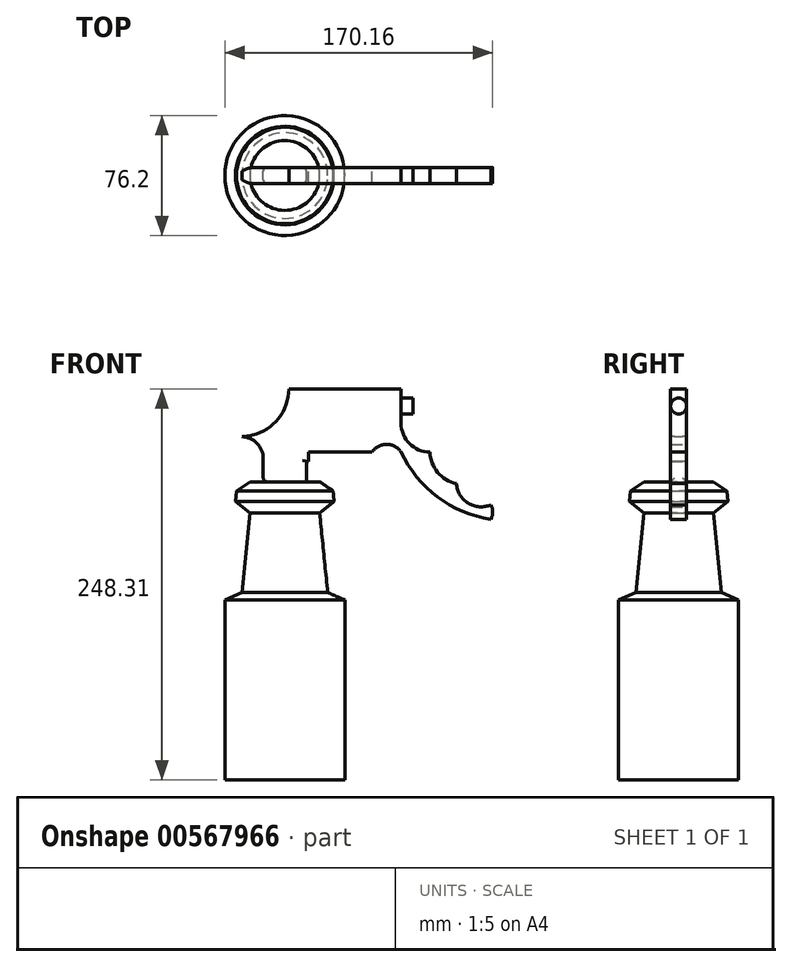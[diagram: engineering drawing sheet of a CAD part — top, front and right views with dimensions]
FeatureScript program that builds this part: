
annotation { "Feature Type Name" : "Feature", "Feature Type Description" : "" }
export const myFeature = defineFeature(function(context is Context, id is Id, definition is map)
    precondition{}
    {
        {
            var Q0;
            Q0=qCreatedBy(makeId("Front.planeOp"),FACE);
            var sketch = newSketch(context, id + "F0", { "sketchPlane" : qUnion([Q0])});
            skLineSegment(sketch, "E0", {"start": v(0, 0) * mm, "end": v(0, 114.3) * mm});
            skLineSegment(sketch, "E1", {"start": v(-38.1, 114.3) * mm, "end": v(-38.1, 0) * mm});
            skLineSegment(sketch, "E2", {"start": v(-38.1, 0) * mm, "end": v(0, 0) * mm});
            skLineSegment(sketch, "E3", {"start": v(0, 114.3) * mm, "end": v(-10.86, 119.11) * mm});
            skLineSegment(sketch, "E4", {"start": v(-38.1, 176.23) * mm, "end": v(-38.1, 114.3) * mm});
            skPoint(sketch, "E5.end.orphan", {"position": v(-25.4, 114.3) * mm});
            skLineSegment(sketch, "E6", {"start": v(-10.86, 119.11) * mm, "end": v(-15.96, 169.65) * mm});
            skLineSegment(sketch, "E7", {"start": v(-15.96, 169.65) * mm, "end": v(-6.76, 176.88) * mm});
            skLineSegment(sketch, "E8", {"start": v(-6.76, 176.88) * mm, "end": v(-7.45, 183.67) * mm});
            skLineSegment(sketch, "E9", {"start": v(-7.45, 183.67) * mm, "end": v(-15.96, 189.42) * mm});
            skLineSegment(sketch, "E10", {"start": v(-15.96, 189.42) * mm, "end": v(-38.1, 189.42) * mm});
            skLineSegment(sketch, "E11", {"start": v(-38.1, 189.42) * mm, "end": v(-38.1, 176.23) * mm});
            skSolve(sketch);
        }
        {
            var Q0;
            Q0=makeQuery(id+"F0.imprint","IMPRINT",FACE,{"disambiguationData":[TD([[makeQuery(id+"F0.imprint","IMPRINT",EDGE,{"derivedFrom":sQuery(id+"F0.wireOp",EDGE,"E0")}),1.0]])]});
            var Q1;
            Q1=sQuery(id+"F0.wireOp",EDGE,"E1");
            revolve(context, id + "F1", {"entities" : qUnion([Q0]), "axis" : qUnion([Q1]), "revolveType" : RevolveType.FULL});
        }
        {
            var Q0;
            Q0=qCreatedBy(makeId("Front.planeOp"),FACE);
            var sketch = newSketch(context, id + "F2", { "sketchPlane" : qUnion([Q0])});
            skLineSegment(sketch, "E12", {"start": v(-51.78, 189.42) * mm, "end": v(-51.78, 204) * mm});
            skArc(sketch, "E13", {"start": v(-51.78, 204) * mm, "mid": v(-56.09, 214.13) * mm, "end": v(-66.37, 218.05) * mm});
            skArc(sketch, "E14", {"start": v(-66.37, 218.05) * mm, "mid": v(-44.65, 226.77) * mm, "end": v(-35.5, 248.3) * mm});
            skLineSegment(sketch, "E15", {"start": v(-35.5, 248.3) * mm, "end": v(35.75, 248.3) * mm});
            skLineSegment(sketch, "E16", {"start": v(35.75, 248.3) * mm, "end": v(35.75, 241.22) * mm});
            skLineSegment(sketch, "E17", {"start": v(35.75, 241.22) * mm, "end": v(35.75, 226.63) * mm});
            skArc(sketch, "E18", {"start": v(35.75, 226.63) * mm, "mid": v(41.13, 213.64) * mm, "end": v(54.12, 208.26) * mm});
            skArc(sketch, "E19", {"start": v(54.12, 208.26) * mm, "mid": v(59.05, 195.38) * mm, "end": v(70.87, 188.27) * mm});
            skArc(sketch, "E20", {"start": v(70.87, 188.27) * mm, "mid": v(78.4, 175.86) * mm, "end": v(92.87, 174.72) * mm});
            skArc(sketch, "E21", {"start": v(92.87, 165.53) * mm, "mid": v(93.96, 170.13) * mm, "end": v(92.87, 174.72) * mm});
            skArc(sketch, "E22", {"start": v(35.75, 208.26) * mm, "mid": v(59, 179.79) * mm, "end": v(92.87, 165.53) * mm});
            skArc(sketch, "E23", {"start": v(35.75, 208.26) * mm, "mid": v(26.57, 213.18) * mm, "end": v(17.38, 208.26) * mm});
            skLineSegment(sketch, "E24", {"start": v(17.38, 208.26) * mm, "end": v(-23.14, 208.26) * mm});
            skLineSegment(sketch, "E25", {"start": v(-23.14, 208.26) * mm, "end": v(-23.14, 202.42) * mm});
            skLineSegment(sketch, "E26", {"start": v(-24.34, 202.6) * mm, "end": v(-23.14, 202.42) * mm});
            skLineSegment(sketch, "E27", {"start": v(-24.34, 202.6) * mm, "end": v(-24.34, 189.42) * mm});
            skLineSegment(sketch, "E28", {"start": v(-51.78, 189.42) * mm, "end": v(-24.34, 189.42) * mm});
            skSolve(sketch);
        }
        {
            var Q0;
            {var subQ0=sQuery(id+"F2.wireOp",EDGE,"E12");Q0=makeQuery(id+"F2.imprint","IMPRINT",FACE,{"disambiguationData":[TD([[makeQuery(id+"F2.imprint","IMPRINT",EDGE,{"derivedFrom":subQ0}),-1.0]])]});}
            extrude(context, id + "F3", {"entities" : qUnion([Q0]), "depth" : 5.08 * mm, "offsetDistance" : 25.4 * mm, "hasSecondDirection" : true, "secondDirectionOppositeDirection" : true, "secondDirectionDepth" : 5.08 * mm});
        }
        {
            var Q0;
            Q0=makeQuery(id+"F3.opExtrude","SWEPT_FACE",FACE,{"disambiguationData":[OSD([sQuery(id+"F2.wireOp",EDGE,"E16"),sQuery(id+"F2.wireOp",EDGE,"E17")])]});
            var sketch = newSketch(context, id + "F4", { "sketchPlane" : qUnion([Q0])});
            skCircle(sketch, "E29", {"center": v(0, 237.47) * mm, "radius": 5.08 * mm});
            skPoint(sketch, "E29.centerSnap0", {"position": v(5.08, 237.47) * mm});
            skSolve(sketch);
        }
        {
            var Q0;
            Q0 = qSketchRegion(id + "F4", true);
            extrude(context, id + "F5", {"entities" : qUnion([Q0]), "operationType" : NewBodyOperationType.ADD, "depth" : 7.62 * mm, "offsetDistance" : 25.4 * mm});
        }
        {
            var Q0;
            Q0=makeQuery(id+"F3.opExtrude","SWEPT_FACE",FACE,{"disambiguationData":[OSD([sQuery(id+"F2.wireOp",EDGE,"E12")])]});
            var Q1;
            Q1=makeQuery(id+"F3.opExtrude","CAP_EDGE",EDGE,{"disambiguationData":[OSD([sQuery(id+"F2.wireOp",EDGE,"E27")])],"isStart":true});
            var Q2;
            Q2=makeQuery(id+"F3.opExtrude","CAP_EDGE",EDGE,{"disambiguationData":[OSD([sQuery(id+"F2.wireOp",EDGE,"E27")])],"isStart":false});
            fillet(context, id + "F6", {"entities" : qUnion([Q0, Q1, Q2]), "radius" : 2.54 * mm, "tangentPropagation" : true, "allowEdgeOverflow" : false});
        }
    });
